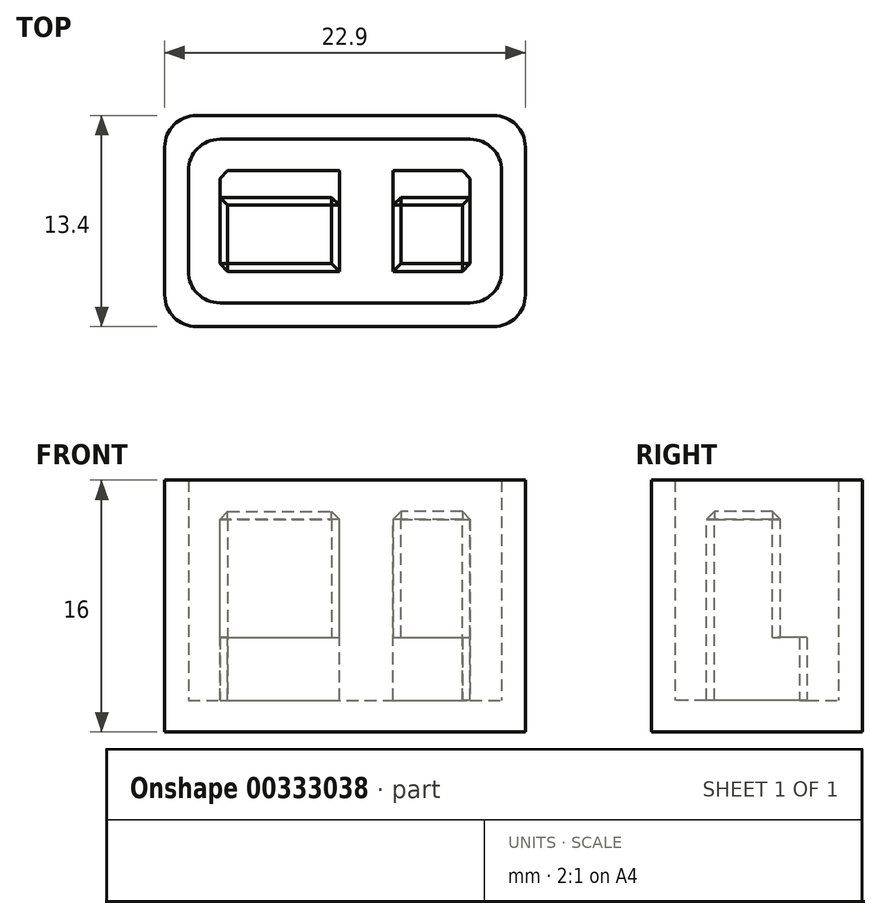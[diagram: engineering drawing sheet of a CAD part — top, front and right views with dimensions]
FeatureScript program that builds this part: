
annotation { "Feature Type Name" : "Feature", "Feature Type Description" : "" }
export const myFeature = defineFeature(function(context is Context, id is Id, definition is map)
    precondition{}
    {
        {
            var Q0;
            Q0=qCreatedBy(makeId("Top.planeOp"),FACE);
            var sketch = newSketch(context, id + "F0", { "sketchPlane" : qUnion([Q0])});
            skLineSegment(sketch, "E0.bottom", {"start": v(-11.45, 6.7) * mm, "end": v(11.45, 6.7) * mm});
            skLineSegment(sketch, "E0.top", {"start": v(-11.45, -6.7) * mm, "end": v(11.45, -6.7) * mm});
            skLineSegment(sketch, "E0.left", {"start": v(-11.45, 6.7) * mm, "end": v(-11.45, -6.7) * mm});
            skLineSegment(sketch, "E0.right", {"start": v(11.45, 6.7) * mm, "end": v(11.45, -6.7) * mm});
            skPoint(sketch, "E0.middle", {"position": v(0, 0) * mm});
            skSolve(sketch);
        }
        {
            var Q0;
            Q0 = qSketchRegion(id + "F0", true);
            extrude(context, id + "F1", {"entities" : qUnion([Q0]), "depth" : 2 * mm});
        }
        {
            var Q0;
            Q0=makeQuery(id+"F1.opExtrude","CAP_FACE",FACE,{"disambiguationData":[OSD([sQuery(id+"F0.wireOp",EDGE,"E0.bottom"),sQuery(id+"F0.wireOp",EDGE,"E0.top"),sQuery(id+"F0.wireOp",EDGE,"E0.left"),sQuery(id+"F0.wireOp",EDGE,"E0.right")])],"isStart":false});
            var sketch = newSketch(context, id + "F2", { "sketchPlane" : qUnion([Q0])});
            skLineSegment(sketch, "E1.bottom", {"start": v(-11.45, 6.7) * mm, "end": v(11.45, 6.7) * mm});
            skLineSegment(sketch, "E1.top", {"start": v(-11.45, -6.7) * mm, "end": v(11.45, -6.7) * mm});
            skLineSegment(sketch, "E1.left", {"start": v(-11.45, 6.7) * mm, "end": v(-11.45, -6.7) * mm});
            skLineSegment(sketch, "E1.right", {"start": v(11.45, 6.7) * mm, "end": v(11.45, -6.7) * mm});
            skPoint(sketch, "E1.middle", {"position": v(0, 0) * mm});
            skLineSegment(sketch, "E2.bottom", {"start": v(-9.95, 5.2) * mm, "end": v(9.95, 5.2) * mm});
            skLineSegment(sketch, "E2.top", {"start": v(-9.95, -5.2) * mm, "end": v(9.95, -5.2) * mm});
            skLineSegment(sketch, "E2.left", {"start": v(-9.95, 5.2) * mm, "end": v(-9.95, -5.2) * mm});
            skLineSegment(sketch, "E2.right", {"start": v(9.95, 5.2) * mm, "end": v(9.95, -5.2) * mm});
            skSolve(sketch);
        }
        {
            var Q0;
            Q0 = qSketchRegion(id + "F2", true);
            extrude(context, id + "F3", {"entities" : qUnion([Q0]), "operationType" : NewBodyOperationType.ADD, "depth" : 14 * mm});
        }
        {
            var Q0;
            Q0=makeQuery(id+"F1.opExtrude","CAP_FACE",FACE,{"disambiguationData":[OSD([sQuery(id+"F0.wireOp",EDGE,"E0.bottom"),sQuery(id+"F0.wireOp",EDGE,"E0.top"),sQuery(id+"F0.wireOp",EDGE,"E0.left"),sQuery(id+"F0.wireOp",EDGE,"E0.right")])],"isStart":false});
            var sketch = newSketch(context, id + "F4", { "sketchPlane" : qUnion([Q0])});
            skLineSegment(sketch, "E3.bottom", {"start": v(-7.95, 3.2) * mm, "end": v(7.95, 3.2) * mm});
            skLineSegment(sketch, "E3.top", {"start": v(-7.95, -3.2) * mm, "end": v(7.95, -3.2) * mm});
            skLineSegment(sketch, "E3.left", {"start": v(-7.95, 3.2) * mm, "end": v(-7.95, -3.2) * mm});
            skLineSegment(sketch, "E3.right", {"start": v(7.95, 3.2) * mm, "end": v(7.95, -3.2) * mm});
            skPoint(sketch, "E3.middle", {"position": v(0, 0) * mm});
            skSolve(sketch);
        }
        {
            var Q0;
            Q0 = qSketchRegion(id + "F4", true);
            extrude(context, id + "F5", {"entities" : qUnion([Q0]), "operationType" : NewBodyOperationType.ADD, "depth" : 12 * mm});
        }
        {
            var Q0;
            Q0=makeQuery(id+"F5.opExtrude","CAP_FACE",FACE,{"disambiguationData":[OSD([sQuery(id+"F4.wireOp",EDGE,"E3.bottom"),sQuery(id+"F4.wireOp",EDGE,"E3.top"),sQuery(id+"F4.wireOp",EDGE,"E3.left"),sQuery(id+"F4.wireOp",EDGE,"E3.right")])],"isStart":false});
            var sketch = newSketch(context, id + "F6", { "sketchPlane" : qUnion([Q0])});
            skLineSegment(sketch, "E4.top", {"start": v(-7.95, 1.5) * mm, "end": v(-0.35, 1.5) * mm});
            skLineSegment(sketch, "E4.left", {"start": v(-7.95, -3.2) * mm, "end": v(-7.95, 1.5) * mm});
            skLineSegment(sketch, "E4.right", {"start": v(-0.35, -3.2) * mm, "end": v(-0.35, 1.5) * mm});
            skLineSegment(sketch, "E5.bottom", {"start": v(3.05, 1.5) * mm, "end": v(7.95, 1.5) * mm});
            skLineSegment(sketch, "E5.left", {"start": v(3.05, 1.5) * mm, "end": v(3.05, -3.2) * mm});
            skLineSegment(sketch, "E5.right", {"start": v(7.95, 1.5) * mm, "end": v(7.95, -3.2) * mm});
            skLineSegment(sketch, "E6", {"start": v(-0.35, 1.5) * mm, "end": v(-0.35, 3.2) * mm});
            skLineSegment(sketch, "E7", {"start": v(3.05, 1.5) * mm, "end": v(3.05, 3.2) * mm});
            skLineSegment(sketch, "E8.bottom", {"start": v(-7.95, 3.2) * mm, "end": v(7.95, 3.2) * mm});
            skLineSegment(sketch, "E8.top", {"start": v(-7.95, -3.2) * mm, "end": v(-7.95, -3.2) * mm});
            skLineSegment(sketch, "E8.left", {"start": v(-7.95, 3.2) * mm, "end": v(-7.95, -3.2) * mm});
            skLineSegment(sketch, "E8.right", {"start": v(7.95, 3.2) * mm, "end": v(7.95, -3.2) * mm});
            skLineSegment(sketch, "E9.trimOffspring", {"start": v(-0.35, -3.2) * mm, "end": v(3.05, -3.2) * mm});
            skLineSegment(sketch, "E10.trimOffspring", {"start": v(7.95, -3.2) * mm, "end": v(7.95, -3.2) * mm});
            skSolve(sketch);
        }
        {
            var Q0;
            Q0 = qSketchRegion(id + "F6", true);
            extrude(context, id + "F7", {"entities" : qUnion([Q0]), "operationType" : NewBodyOperationType.REMOVE, "oppositeDirection" : true, "depth" : 8 * mm});
        }
        {
            var Q0;
            Q0=makeQuery(id+"F7.boolean.opBoolean","COPY",FACE,{"derivedFrom":makeQuery(id+"F7.opExtrude","CAP_FACE",FACE,{"disambiguationData":[OSD([sQuery(id+"F6.wireOp",EDGE,"E4.top"),sQuery(id+"F6.wireOp",EDGE,"E4.left"),sQuery(id+"F6.wireOp",EDGE,"E4.right"),sQuery(id+"F6.wireOp",EDGE,"E5.bottom"),sQuery(id+"F6.wireOp",EDGE,"E5.left"),sQuery(id+"F6.wireOp",EDGE,"E5.right"),sQuery(id+"F6.wireOp",EDGE,"E8.bottom"),sQuery(id+"F6.wireOp",EDGE,"E8.top"),sQuery(id+"F6.wireOp",EDGE,"E8.left"),sQuery(id+"F6.wireOp",EDGE,"E8.right"),sQuery(id+"F6.wireOp",EDGE,"E9.trimOffspring"),sQuery(id+"F6.wireOp",EDGE,"E10.trimOffspring")])],"isStart":false})});
            var sketch = newSketch(context, id + "F8", { "sketchPlane" : qUnion([Q0])});
            skLineSegment(sketch, "E11.bottom", {"start": v(-0.35, 3.2) * mm, "end": v(3.05, 3.2) * mm});
            skLineSegment(sketch, "E11.top", {"start": v(-0.35, -3.2) * mm, "end": v(3.05, -3.2) * mm});
            skLineSegment(sketch, "E11.left", {"start": v(-0.35, 3.2) * mm, "end": v(-0.35, -3.2) * mm});
            skLineSegment(sketch, "E11.right", {"start": v(3.05, 3.2) * mm, "end": v(3.05, -3.2) * mm});
            skSolve(sketch);
        }
        {
            var Q0;
            Q0 = qSketchRegion(id + "F8", true);
            extrude(context, id + "F9", {"entities" : qUnion([Q0]), "operationType" : NewBodyOperationType.REMOVE, "oppositeDirection" : true, "depth" : 4 * mm});
        }
        {
            var Q0;
            {var subQ0=sQuery(id+"F4.wireOp",EDGE,"E3.top");Q0=makeQuery(id+"F7.boolean.opBoolean","SPLIT",FACE,{"disambiguationData":[TD([makeQuery(id+"F7.opExtrude","SWEPT_FACE",FACE,{"disambiguationData":[OSD([sQuery(id+"F6.wireOp",EDGE,"E4.top")])]})])],"derivedFrom":makeQuery(id+"F5.opExtrude","CAP_FACE",FACE,{"disambiguationData":[OSD([sQuery(id+"F4.wireOp",EDGE,"E3.bottom"),subQ0,sQuery(id+"F4.wireOp",EDGE,"E3.left"),sQuery(id+"F4.wireOp",EDGE,"E3.right")])],"isStart":false})});}
            var Q1;
            Q1=makeQuery(id+"F7.boolean.opBoolean","COPY",EDGE,{"derivedFrom":makeQuery(id+"F7.opExtrude","SWEPT_EDGE",EDGE,{"disambiguationData":[OSD([sQuery(id+"F4.wireOp",EDGE,"E3.top"),sQuery(id+"F6.wireOp",EDGE,"E4.left"),sQuery(id+"F6.wireOp",EDGE,"E8.top")])]})});
            var Q2;
            Q2=makeQuery(id+"F7.boolean.opBoolean","COPY",EDGE,{"derivedFrom":makeQuery(id+"F7.opExtrude","SWEPT_EDGE",EDGE,{"disambiguationData":[OSD([sQuery(id+"F6.wireOp",EDGE,"E4.top"),sQuery(id+"F6.wireOp",EDGE,"E4.left")])]})});
            var Q3;
            Q3=makeQuery(id+"F7.boolean.opBoolean","COPY",EDGE,{"derivedFrom":makeQuery(id+"F7.opExtrude","SWEPT_EDGE",EDGE,{"disambiguationData":[OSD([sQuery(id+"F6.wireOp",EDGE,"E4.top"),sQuery(id+"F6.wireOp",EDGE,"E4.right"),sQuery(id+"F6.wireOp",EDGE,"E6")])]})});
            var Q4;
            Q4=makeQuery(id+"F7.boolean.opBoolean","COPY",EDGE,{"derivedFrom":makeQuery(id+"F7.opExtrude","SWEPT_EDGE",EDGE,{"disambiguationData":[OSD([sQuery(id+"F4.wireOp",EDGE,"E3.top"),sQuery(id+"F6.wireOp",EDGE,"E4.right"),sQuery(id+"F6.wireOp",EDGE,"E9.trimOffspring")])]})});
            var Q5;
            Q5=makeQuery(id+"F7.boolean.opBoolean","COPY",EDGE,{"derivedFrom":makeQuery(id+"F7.opExtrude","SWEPT_EDGE",EDGE,{"disambiguationData":[OSD([sQuery(id+"F4.wireOp",EDGE,"E3.top"),sQuery(id+"F6.wireOp",EDGE,"E5.left"),sQuery(id+"F6.wireOp",EDGE,"E9.trimOffspring")])]})});
            var Q6;
            {var subQ0=sQuery(id+"F4.wireOp",EDGE,"E3.top");Q6=makeQuery(id+"F7.boolean.opBoolean","SPLIT",FACE,{"disambiguationData":[TD([makeQuery(id+"F7.opExtrude","SWEPT_FACE",FACE,{"disambiguationData":[OSD([sQuery(id+"F6.wireOp",EDGE,"E5.bottom")])]})])],"derivedFrom":makeQuery(id+"F5.opExtrude","CAP_FACE",FACE,{"disambiguationData":[OSD([sQuery(id+"F4.wireOp",EDGE,"E3.bottom"),subQ0,sQuery(id+"F4.wireOp",EDGE,"E3.left"),sQuery(id+"F4.wireOp",EDGE,"E3.right")])],"isStart":false})});}
            var Q7;
            Q7=makeQuery(id+"F7.boolean.opBoolean","COPY",EDGE,{"derivedFrom":makeQuery(id+"F7.opExtrude","SWEPT_EDGE",EDGE,{"disambiguationData":[OSD([sQuery(id+"F4.wireOp",EDGE,"E3.top"),sQuery(id+"F6.wireOp",EDGE,"E5.right"),sQuery(id+"F6.wireOp",EDGE,"E10.trimOffspring")])]})});
            var Q8;
            Q8=makeQuery(id+"F7.boolean.opBoolean","COPY",EDGE,{"derivedFrom":makeQuery(id+"F7.opExtrude","SWEPT_EDGE",EDGE,{"disambiguationData":[OSD([sQuery(id+"F6.wireOp",EDGE,"E5.bottom"),sQuery(id+"F6.wireOp",EDGE,"E5.right")])]})});
            var Q9;
            Q9=makeQuery(id+"F7.boolean.opBoolean","COPY",EDGE,{"derivedFrom":makeQuery(id+"F7.opExtrude","SWEPT_EDGE",EDGE,{"disambiguationData":[OSD([sQuery(id+"F6.wireOp",EDGE,"E5.bottom"),sQuery(id+"F6.wireOp",EDGE,"E5.left"),sQuery(id+"F6.wireOp",EDGE,"E7")])]})});
            var Q10;
            Q10=makeQuery(id+"F9.boolean.opBoolean","COPY",EDGE,{"derivedFrom":makeQuery(id+"F9.opExtrude","SWEPT_EDGE",EDGE,{"disambiguationData":[OSD([sQuery(id+"F6.wireOp",EDGE,"E9.trimOffspring"),sQuery(id+"F8.wireOp",EDGE,"E11.top"),sQuery(id+"F8.wireOp",EDGE,"E11.left")])]})});
            var Q11;
            Q11=makeQuery(id+"F9.boolean.opBoolean","COPY",EDGE,{"derivedFrom":makeQuery(id+"F9.opExtrude","SWEPT_EDGE",EDGE,{"disambiguationData":[OSD([sQuery(id+"F6.wireOp",EDGE,"E9.trimOffspring"),sQuery(id+"F8.wireOp",EDGE,"E11.top"),sQuery(id+"F8.wireOp",EDGE,"E11.right")])]})});
            var Q12;
            Q12=makeQuery(id+"F9.boolean.opBoolean","COPY",EDGE,{"derivedFrom":makeQuery(id+"F9.opExtrude","SWEPT_EDGE",EDGE,{"disambiguationData":[OSD([sQuery(id+"F6.wireOp",EDGE,"E8.bottom"),sQuery(id+"F8.wireOp",EDGE,"E11.bottom"),sQuery(id+"F8.wireOp",EDGE,"E11.right")])]})});
            var Q13;
            Q13=makeQuery(id+"F5.opExtrude","SWEPT_EDGE",EDGE,{"disambiguationData":[OSD([sQuery(id+"F4.wireOp",EDGE,"E3.bottom"),sQuery(id+"F4.wireOp",EDGE,"E3.right")])]});
            var Q14;
            Q14=makeQuery(id+"F5.opExtrude","SWEPT_EDGE",EDGE,{"disambiguationData":[OSD([sQuery(id+"F4.wireOp",EDGE,"E3.top"),sQuery(id+"F4.wireOp",EDGE,"E3.right")])]});
            var Q15;
            Q15=makeQuery(id+"F9.boolean.opBoolean","COPY",EDGE,{"derivedFrom":makeQuery(id+"F9.opExtrude","SWEPT_EDGE",EDGE,{"disambiguationData":[OSD([sQuery(id+"F6.wireOp",EDGE,"E8.bottom"),sQuery(id+"F8.wireOp",EDGE,"E11.bottom"),sQuery(id+"F8.wireOp",EDGE,"E11.left")])]})});
            var Q16;
            Q16=makeQuery(id+"F5.opExtrude","SWEPT_EDGE",EDGE,{"disambiguationData":[OSD([sQuery(id+"F4.wireOp",EDGE,"E3.bottom"),sQuery(id+"F4.wireOp",EDGE,"E3.left")])]});
            var Q17;
            Q17=makeQuery(id+"F5.opExtrude","SWEPT_EDGE",EDGE,{"disambiguationData":[OSD([sQuery(id+"F4.wireOp",EDGE,"E3.top"),sQuery(id+"F4.wireOp",EDGE,"E3.left")])]});
            chamfer(context, id + "F10", {"entities" : qUnion([Q0, Q1, Q2, Q3, Q4, Q5, Q6, Q7, Q8, Q9, Q10, Q11, Q12, Q13, Q14, Q15, Q16, Q17]), "width" : .5 * mm, "tangentPropagation" : true});
        }
        {
            var Q0;
            Q0=makeQuery(id+"F3.opExtrude","SWEPT_EDGE",EDGE,{"disambiguationData":[OSD([sQuery(id+"F2.wireOp",EDGE,"E2.top"),sQuery(id+"F2.wireOp",EDGE,"E2.right")])]});
            var Q1;
            Q1=makeQuery(id+"F3.opExtrude","SWEPT_EDGE",EDGE,{"disambiguationData":[OSD([sQuery(id+"F2.wireOp",EDGE,"E2.bottom"),sQuery(id+"F2.wireOp",EDGE,"E2.right")])]});
            var Q2;
            Q2=makeQuery(id+"F3.opExtrude","SWEPT_EDGE",EDGE,{"disambiguationData":[OSD([sQuery(id+"F2.wireOp",EDGE,"E2.bottom"),sQuery(id+"F2.wireOp",EDGE,"E2.left")])]});
            var Q3;
            Q3=makeQuery(id+"F3.opExtrude","SWEPT_EDGE",EDGE,{"disambiguationData":[OSD([sQuery(id+"F2.wireOp",EDGE,"E2.top"),sQuery(id+"F2.wireOp",EDGE,"E2.left")])]});
            var Q4;
            Q4=makeQuery(id+"F3.boolean.opBoolean","MERGE",EDGE,{"derivedFrom":[makeQuery(id+"F1.opExtrude","SWEPT_EDGE",EDGE,{"disambiguationData":[OSD([sQuery(id+"F0.wireOp",EDGE,"E0.top"),sQuery(id+"F0.wireOp",EDGE,"E0.right")])]}),makeQuery(id+"F3.opExtrude","SWEPT_EDGE",EDGE,{"disambiguationData":[OSD([sQuery(id+"F2.wireOp",EDGE,"E1.top"),sQuery(id+"F2.wireOp",EDGE,"E1.right")])]})]});
            var Q5;
            Q5=makeQuery(id+"F3.boolean.opBoolean","MERGE",EDGE,{"derivedFrom":[makeQuery(id+"F1.opExtrude","SWEPT_EDGE",EDGE,{"disambiguationData":[OSD([sQuery(id+"F0.wireOp",EDGE,"E0.bottom"),sQuery(id+"F0.wireOp",EDGE,"E0.right")])]}),makeQuery(id+"F3.opExtrude","SWEPT_EDGE",EDGE,{"disambiguationData":[OSD([sQuery(id+"F2.wireOp",EDGE,"E1.bottom"),sQuery(id+"F2.wireOp",EDGE,"E1.right")])]})]});
            var Q6;
            Q6=makeQuery(id+"F3.boolean.opBoolean","MERGE",EDGE,{"derivedFrom":[makeQuery(id+"F1.opExtrude","SWEPT_EDGE",EDGE,{"disambiguationData":[OSD([sQuery(id+"F0.wireOp",EDGE,"E0.bottom"),sQuery(id+"F0.wireOp",EDGE,"E0.left")])]}),makeQuery(id+"F3.opExtrude","SWEPT_EDGE",EDGE,{"disambiguationData":[OSD([sQuery(id+"F2.wireOp",EDGE,"E1.bottom"),sQuery(id+"F2.wireOp",EDGE,"E1.left")])]})]});
            var Q7;
            Q7=makeQuery(id+"F3.boolean.opBoolean","MERGE",EDGE,{"derivedFrom":[makeQuery(id+"F1.opExtrude","SWEPT_EDGE",EDGE,{"disambiguationData":[OSD([sQuery(id+"F0.wireOp",EDGE,"E0.top"),sQuery(id+"F0.wireOp",EDGE,"E0.left")])]}),makeQuery(id+"F3.opExtrude","SWEPT_EDGE",EDGE,{"disambiguationData":[OSD([sQuery(id+"F2.wireOp",EDGE,"E1.top"),sQuery(id+"F2.wireOp",EDGE,"E1.left")])]})]});
            fillet(context, id + "F11", {"entities" : qUnion([Q0, Q1, Q2, Q3, Q4, Q5, Q6, Q7]), "radius" : 2 * mm, "tangentPropagation" : true, "allowEdgeOverflow" : false});
        }
    });
